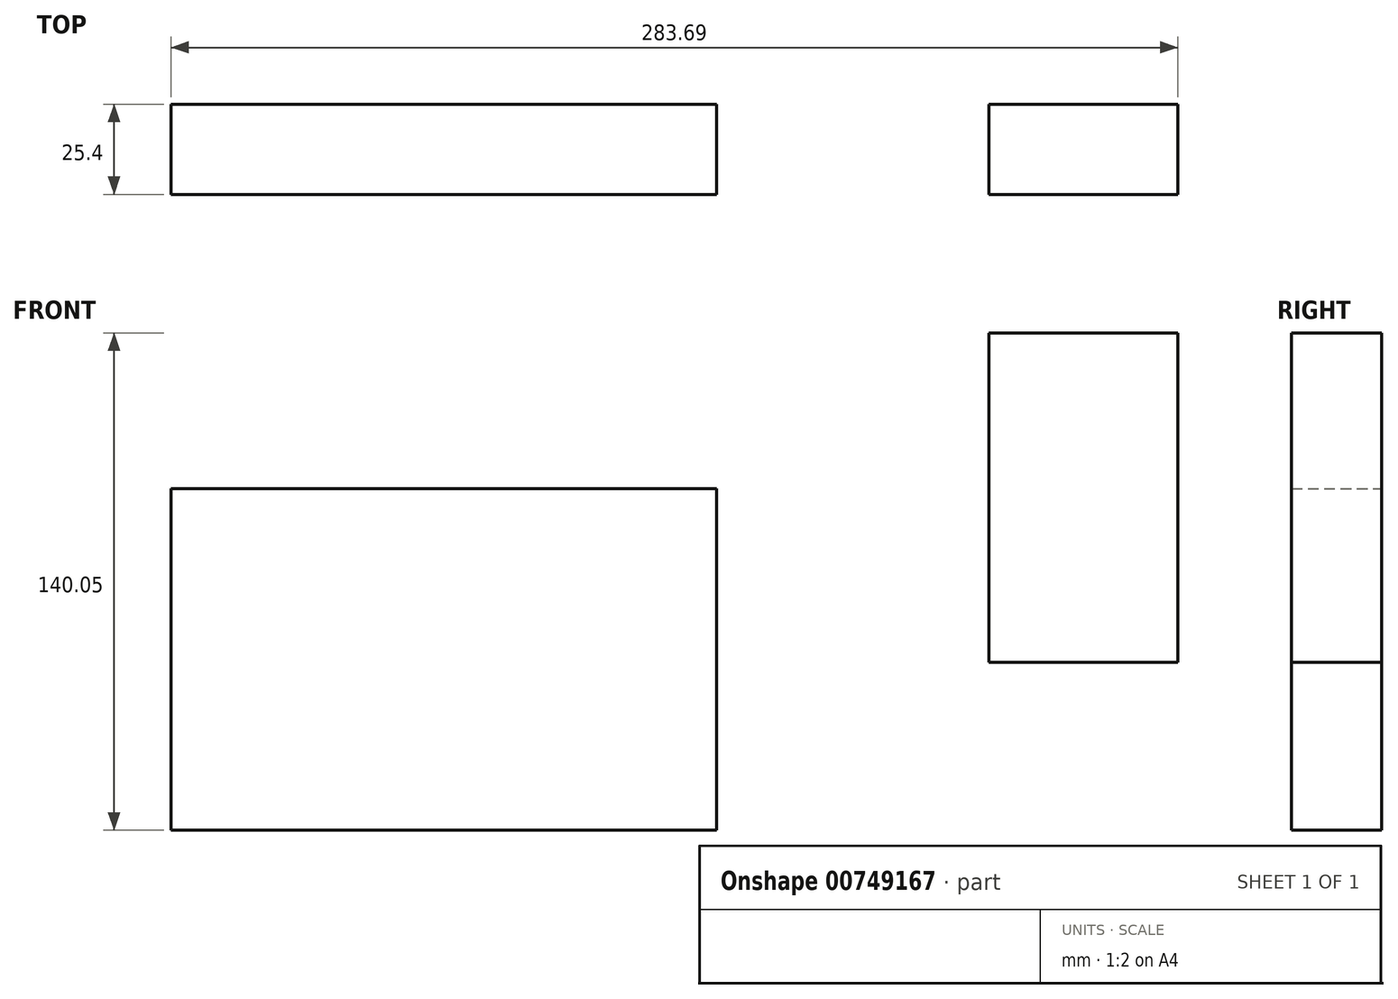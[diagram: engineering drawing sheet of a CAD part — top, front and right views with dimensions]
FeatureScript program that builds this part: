
annotation { "Feature Type Name" : "Feature", "Feature Type Description" : "" }
export const myFeature = defineFeature(function(context is Context, id is Id, definition is map)
    precondition{}
    {
        {
            var Q0;
            Q0=qCreatedBy(makeId("Front.planeOp"),FACE);
            var sketch = newSketch(context, id + "F0", { "sketchPlane" : qUnion([Q0])});
            skLineSegment(sketch, "E0.bottom", {"start": v(-32.95, 71.58) * mm, "end": v(120.74, 71.58) * mm});
            skLineSegment(sketch, "E0.top", {"start": v(-32.95, -24.61) * mm, "end": v(120.74, -24.61) * mm});
            skLineSegment(sketch, "E0.left", {"start": v(-32.95, 71.58) * mm, "end": v(-32.95, -24.61) * mm});
            skLineSegment(sketch, "E0.right", {"start": v(120.74, 71.58) * mm, "end": v(120.74, -24.61) * mm});
            skLineSegment(sketch, "E1.bottom", {"start": v(197.45, 115.44) * mm, "end": v(250.74, 115.44) * mm});
            skLineSegment(sketch, "E1.top", {"start": v(197.45, 22.7) * mm, "end": v(250.74, 22.7) * mm});
            skLineSegment(sketch, "E1.left", {"start": v(197.45, 115.44) * mm, "end": v(197.45, 22.7) * mm});
            skLineSegment(sketch, "E1.right", {"start": v(250.74, 115.44) * mm, "end": v(250.74, 22.7) * mm});
            skSolve(sketch);
        }
        {
            var Q0;
            Q0 = qSketchRegion(id + "F0", true);
            extrude(context, id + "F1", {"entities" : qUnion([Q0]), "depth" : 25.4 * mm, "offsetDistance" : 25.4 * mm});
        }
    });
